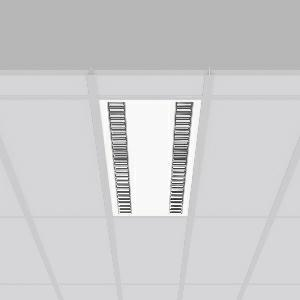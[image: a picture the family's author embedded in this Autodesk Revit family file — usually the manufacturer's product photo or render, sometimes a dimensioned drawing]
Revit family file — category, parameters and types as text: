
# Revit family: sonis_901680_002_1_76_fe08
name_source: partatom
category: Lighting Fixtures
units: mm (PartAtom-declared; Revit-internal decimal feet)

## family parameters
Cut with Voids When Loaded = No
Host = Face
Light Source = No
Part Type = Normal
Room Calculation Point = No
Round Connector Dimension = Use Diameter
Shared = No

## types (1)
- SONIS (1 x LED Modul 840, 6500 lm, 4000)
    Apparent Load = 50 VA
    CIE Flux Codes = 83 100 100 100 100
    Color Rendering = 80
    Color Temperature = 4000
    Default Elevation = 1800 mm
    Description = Series: SONIS
High-efficiency lay-in luminaire for ceiling systems with visible mounting rails. Housing: metal, powder-coated. Alea optical system: Reflector structure (ABS, Aluminium-coated, highly polished) with integrated diffuser made of non-yellowing plastic (PMMA) opal for glare-free light at the workstation. Narrow beam, brilliant luminous effect. Suitable for Recessed ceiling mounting. Driver integrated. Perfect for office areas (RUG < 19) and environments with computer screens in accordance with EN 12464-1. 
Colour: white
Length: 1197 mm
Width: 297 mm
Cut-out length: 1175 mm
Cut-out width: 275 mm
Recess height: 27 mm
Lamp: LED
Socket: without socket
Colour temperature: 4000K
Colour rendering index (CRI): 80
System power: 50 W
Rated luminous flux: 6500 lm
Luminous efficiency: 130 lm/W
Control gear: Converter, dimmable, DALI
Protection class: I
Type of protection: IP 20
    Height = 0 mm  [stored 0 ft]
    Lamp = 1 x LED Modul 840
    Lamp Light Flux = 6500 lm
    Lamp count = 1
    Length = 1197 mm
    Lifetime = 50000 h
    Luminous efficacy = 130 lm/W
    Manufacturer = RZB
    ModVariant = No
    Model = 901680.002.1.76
    Mounting Place = Ceiling
    Mounting Type = Recessed
    Number of Poles = 1
    OnlyDefault = Yes
    Power Factor = 1
    Product Name = SONIS
    Product group = Recessed modular luminaires
    ProductGroupID = 406
    Protection Class = Protection class I
    Protection Degree = IP 20
    RLX_Detail_Level = 1
    RLX_Emergency_Light_Flux = 0 lm
    RLX_Emergency_Type = 0
    RLX_Emergency_Type_DB = No
    RlxData = <blob elided: 37605 chars, md5=54933a71>
    Socket = socket
    Standby Power = 0 W
    System Light Flux = 6500 lm
    System Power = 50 W
    Type Comments = Product without accessories
    Type Image = 901648.002.jpg
    URL = http://relux.com
    VarID = ---
    Voltage = 230 V
    Voltage Range = 220-240 V
    Weight = 0.00 kg
    Width = 297 mm

note: [stored X ft] marks values corroborated as IEEE doubles in the binary element streams (Revit-internal decimal feet)

## geometry (parser evidence)
native form markers: Blend x4, Sweep x12
no freeform markers — native parametric forms only
